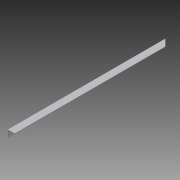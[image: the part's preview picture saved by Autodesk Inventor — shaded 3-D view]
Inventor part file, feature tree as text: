
AUTODESK INVENTOR PART (.ipt)
format: ipt  version: 2014 (Build 180170000, 170)  size: 81,920 bytes
history: native  units: in
note: dims shown in document units (in); Inventor stores cm internally (conversion verified against a paired STEP export)
features: extrude x2, sketch x2
ambient origin geometry x8: Origin, YZ Plane, XZ Plane, XY Plane, X Axis, Y Axis, Z Axis, Center Point
bodies: Solid1 (feature_tree)
feature tree (4):
  extrude  "Extrusion1"  Depth=0.5in
  extrude  "Extrusion2"  Depth=0.45in
  sketch  "Sketch1"  dims[d0=0.5in d1=0.5in]
  sketch  "Sketch2"  dims[d2=0.05in d3=0.45in d4=11.5in d5=0.0in d6=45.0deg d8=9.0in d9=0.0in]
